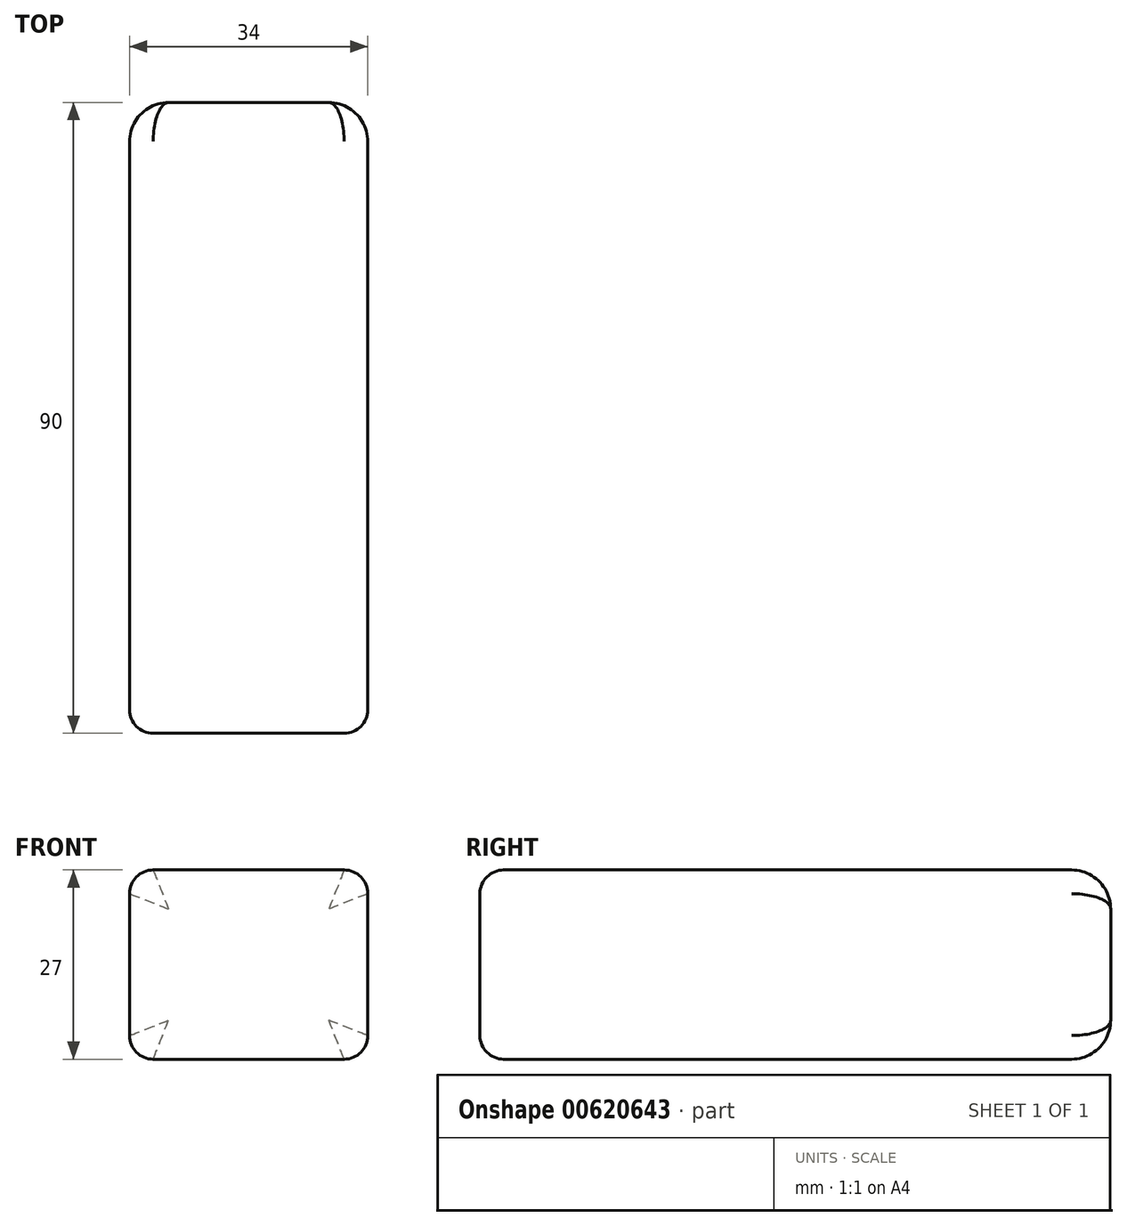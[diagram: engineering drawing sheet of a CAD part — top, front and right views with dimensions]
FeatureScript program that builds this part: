
annotation { "Feature Type Name" : "Feature", "Feature Type Description" : "" }
export const myFeature = defineFeature(function(context is Context, id is Id, definition is map)
    precondition{}
    {
        {
            var Q0;
            Q0=qCreatedBy(makeId("Top.planeOp"),FACE);
            var sketch = newSketch(context, id + "F0", { "sketchPlane" : qUnion([Q0])});
            skLineSegment(sketch, "E0.bottom", {"start": v(-16.1, 48.3) * mm, "end": v(17.9, 48.3) * mm});
            skLineSegment(sketch, "E0.top", {"start": v(-16.1, -41.7) * mm, "end": v(17.9, -41.7) * mm});
            skLineSegment(sketch, "E0.left", {"start": v(-16.1, 48.3) * mm, "end": v(-16.1, -41.7) * mm});
            skLineSegment(sketch, "E0.right", {"start": v(17.9, 48.3) * mm, "end": v(17.9, -41.7) * mm});
            skPoint(sketch, "E0.middle", {"position": v(0.9, 3.3) * mm});
            skSolve(sketch);
        }
        {
            var Q0;
            Q0=makeQuery(id+"F0.imprint","IMPRINT",FACE,{"disambiguationData":[TD([[makeQuery(id+"F0.imprint","IMPRINT",EDGE,{"derivedFrom":sQuery(id+"F0.wireOp",EDGE,"E0.bottom")}),-1.0]])]});
            extrude(context, id + "F1", {"entities" : qUnion([Q0]), "depth" : 27 * mm, "offsetDistance" : 25 * mm});
        }
        {
            var Q0;
            Q0=makeQuery(id+"F1.opExtrude","CAP_EDGE",EDGE,{"disambiguationData":[OSD([sQuery(id+"F0.wireOp",EDGE,"E0.right")])],"isStart":false});
            var Q1;
            Q1=makeQuery(id+"F1.opExtrude","CAP_EDGE",EDGE,{"disambiguationData":[OSD([sQuery(id+"F0.wireOp",EDGE,"E0.left")])],"isStart":true});
            var Q2;
            Q2=makeQuery(id+"F1.opExtrude","CAP_EDGE",EDGE,{"disambiguationData":[OSD([sQuery(id+"F0.wireOp",EDGE,"E0.left")])],"isStart":false});
            var Q3;
            Q3=makeQuery(id+"F1.opExtrude","CAP_EDGE",EDGE,{"disambiguationData":[OSD([sQuery(id+"F0.wireOp",EDGE,"E0.right")])],"isStart":true});
            var Q4;
            Q4=makeQuery(id+"F1.opExtrude","CAP_EDGE",EDGE,{"disambiguationData":[OSD([sQuery(id+"F0.wireOp",EDGE,"E0.top")])],"isStart":false});
            var Q5;
            Q5=makeQuery(id+"F1.opExtrude","CAP_EDGE",EDGE,{"disambiguationData":[OSD([sQuery(id+"F0.wireOp",EDGE,"E0.top")])],"isStart":true});
            var Q6;
            Q6=makeQuery(id+"F1.opExtrude","SWEPT_EDGE",EDGE,{"disambiguationData":[OSD([sQuery(id+"F0.wireOp",EDGE,"E0.top"),sQuery(id+"F0.wireOp",EDGE,"E0.left")])]});
            var Q7;
            Q7=makeQuery(id+"F1.opExtrude","SWEPT_EDGE",EDGE,{"disambiguationData":[OSD([sQuery(id+"F0.wireOp",EDGE,"E0.top"),sQuery(id+"F0.wireOp",EDGE,"E0.right")])]});
            fillet(context, id + "F2", {"entities" : qUnion([Q0, Q1, Q2, Q3, Q4, Q5, Q6, Q7]), "radius" : 3.38 * mm, "tangentPropagation" : true, "allowEdgeOverflow" : false});
        }
        {
            var Q0;
            Q0=makeQuery(id+"F1.opExtrude","CAP_EDGE",EDGE,{"disambiguationData":[OSD([sQuery(id+"F0.wireOp",EDGE,"E0.bottom")])],"isStart":false});
            fillet(context, id + "F3", {"entities" : qUnion([Q0]), "radius" : 5.55 * mm, "tangentPropagation" : true, "allowEdgeOverflow" : false});
        }
    });
